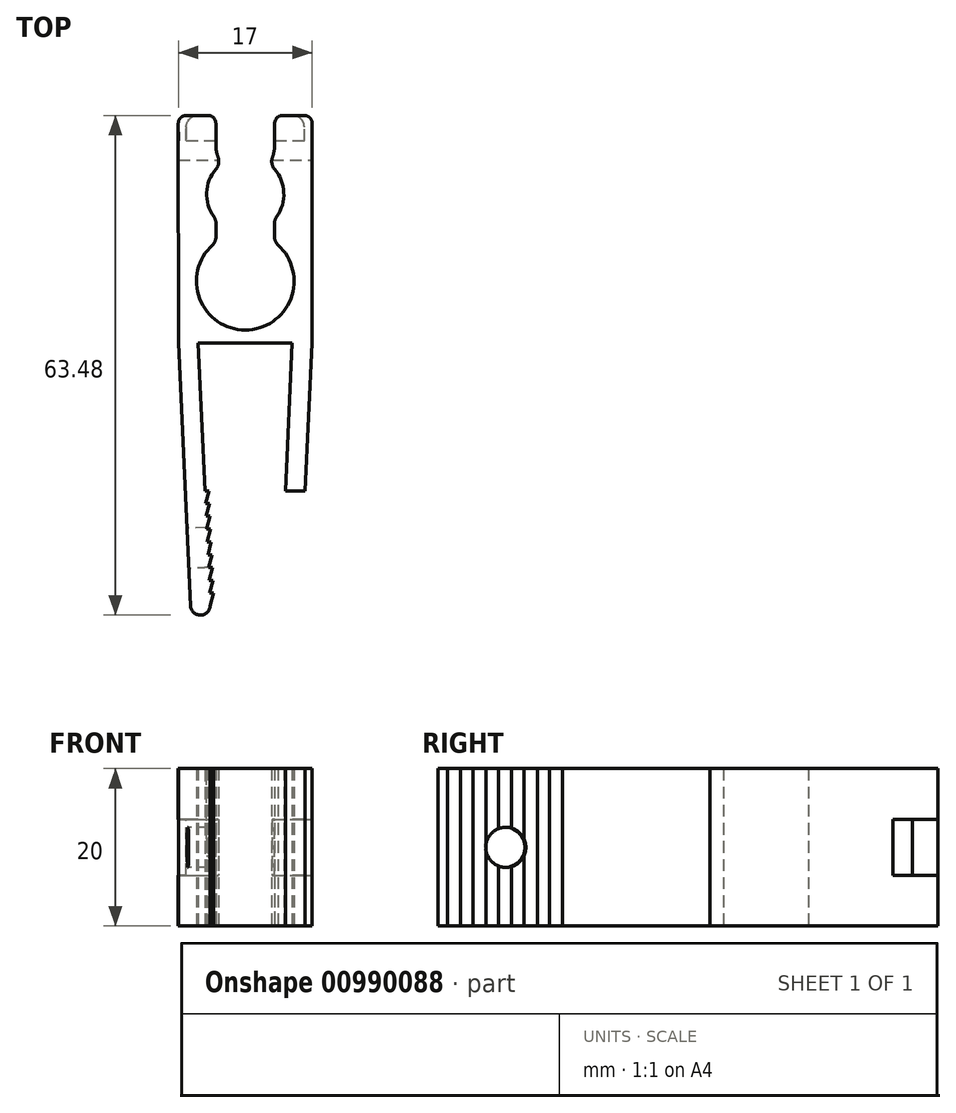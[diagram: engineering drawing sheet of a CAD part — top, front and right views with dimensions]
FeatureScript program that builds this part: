
annotation { "Feature Type Name" : "Feature", "Feature Type Description" : "" }
export const myFeature = defineFeature(function(context is Context, id is Id, definition is map)
    precondition{}
    {
        {
            var Q0;
            Q0=qCreatedBy(makeId("Top.planeOp"),FACE);
            var sketch = newSketch(context, id + "F0", { "sketchPlane" : qUnion([Q0])});
            skPoint(sketch, "E0.MirrorCS.start.orphan", {"position": v(12.82, 0) * mm});
            skLineSegment(sketch, "E1.MirrorCS", {"start": v(-8.47, 46.35) * mm, "end": v(-8.5, 70.8) * mm});
            skPoint(sketch, "E2.MirrorCS.start.orphan", {"position": v(0, 0) * mm});
            skLineSegment(sketch, "E3", {"start": v(0, 49.57) * mm, "end": v(0, 48.03) * mm});
            skLineSegment(sketch, "E4", {"start": v(0, 46.35) * mm, "end": v(5.97, 46.35) * mm});
            skLineSegment(sketch, "E5", {"start": v(0, 46.35) * mm, "end": v(-5.97, 46.35) * mm});
            skLineSegment(sketch, "E6", {"start": v(0, 65.28) * mm, "end": v(0, 49.27) * mm, "construction": true});
            skArc(sketch, "E7", {"start": v(-3.73, 68.46) * mm, "mid": v(-4.9, 65.5) * mm, "end": v(-4, 62.44) * mm});
            skPoint(sketch, "E8.visualSharp", {"position": v(8.5, 0) * mm});
            skPoint(sketch, "E9.visualSharp", {"position": v(-8.5, 0) * mm});
            skLineSegment(sketch, "E10", {"start": v(0, 65.28) * mm, "end": v(0, 75.2) * mm, "construction": true});
            skLineSegment(sketch, "E11.MirrorCS", {"start": v(8.47, 46.35) * mm, "end": v(8.5, 70.8) * mm});
            skPoint(sketch, "E12.orphan", {"position": v(-6, 0) * mm});
            skPoint(sketch, "E13.trimOffspring.start.orphan", {"position": v(6, 0) * mm});
            skPoint(sketch, "E14.visualSharp", {"position": v(-8.5, 10.27) * mm});
            skLineSegment(sketch, "E15", {"start": v(3.71, 61.57) * mm, "end": v(3.71, 59.9) * mm});
            skArc(sketch, "E16.trimOffspring", {"start": v(4, 62.44) * mm, "mid": v(4.9, 65.5) * mm, "end": v(3.73, 68.46) * mm});
            skPoint(sketch, "E17.visualSharp", {"position": v(3.71, 62.08) * mm});
            skArc(sketch, "E17.filletArc", {"start": v(4, 62.44) * mm, "mid": v(3.79, 62.02) * mm, "end": v(3.71, 61.57) * mm});
            skArc(sketch, "E18.filletArc", {"start": v(3.71, 59.9) * mm, "mid": v(3.83, 59.32) * mm, "end": v(4.15, 58.84) * mm});
            skArc(sketch, "E19.MirrorCS", {"start": v(-4, 62.44) * mm, "mid": v(-3.79, 62.02) * mm, "end": v(-3.71, 61.57) * mm});
            skLineSegment(sketch, "E20.MirrorCS", {"start": v(-3.71, 61.57) * mm, "end": v(-3.71, 59.9) * mm});
            skArc(sketch, "E21.MirrorCS", {"start": v(-3.71, 59.9) * mm, "mid": v(-3.83, 59.32) * mm, "end": v(-4.15, 58.84) * mm});
            skArc(sketch, "E22.trimOffspring", {"start": v(-4.15, 58.84) * mm, "mid": v(0, 48.03) * mm, "end": v(4.15, 58.84) * mm});
            skPoint(sketch, "E23.center.orphan", {"position": v(0, 54.53) * mm});
            skArc(sketch, "E24.filletArc", {"start": v(3.74, 70.42) * mm, "mid": v(3.37, 69.45) * mm, "end": v(3.73, 68.46) * mm});
            skArc(sketch, "E25.MirrorCS", {"start": v(-3.45, 69.94) * mm, "mid": v(-3.4, 69.16) * mm, "end": v(-3.73, 68.46) * mm});
            skPoint(sketch, "E26.orphan", {"position": v(-8.47, 46.35) * mm});
            skLineSegment(sketch, "E27", {"start": v(-5.97, 46.35) * mm, "end": v(-5.12, 27.58) * mm});
            skLineSegment(sketch, "E28", {"start": v(-8.47, 46.35) * mm, "end": v(-6.95, 13) * mm});
            skArc(sketch, "E29", {"start": v(-6.95, 13) * mm, "mid": v(-5.7, 11.81) * mm, "end": v(-4.45, 13) * mm});
            skArc(sketch, "E30.MirrorCS", {"start": v(6.95, 13) * mm, "mid": v(5.7, 11.81) * mm, "end": v(4.45, 13) * mm});
            skLineSegment(sketch, "E31.MirrorCS", {"start": v(8.47, 46.35) * mm, "end": v(6.95, 13) * mm});
            skLineSegment(sketch, "E32.MirrorCS", {"start": v(5.97, 46.35) * mm, "end": v(5.12, 27.58) * mm});
            skLineSegment(sketch, "E33", {"start": v(-4.45, 13) * mm, "end": v(-4.03, 14.62) * mm});
            skLineSegment(sketch, "E34", {"start": v(-4.03, 14.62) * mm, "end": v(-4.52, 14.62) * mm});
            skLineSegment(sketch, "E35", {"start": v(-4.52, 14.62) * mm, "end": v(-4.1, 16.24) * mm});
            skLineSegment(sketch, "E36", {"start": v(-4.1, 16.24) * mm, "end": v(-4.59, 16.24) * mm});
            skLineSegment(sketch, "E37", {"start": v(-4.59, 16.24) * mm, "end": v(-4.17, 17.86) * mm});
            skLineSegment(sketch, "E38", {"start": v(-4.17, 17.86) * mm, "end": v(-4.67, 17.86) * mm});
            skLineSegment(sketch, "E39", {"start": v(-4.67, 17.86) * mm, "end": v(-4.25, 19.48) * mm});
            skLineSegment(sketch, "E40", {"start": v(-4.25, 19.48) * mm, "end": v(-4.75, 19.48) * mm});
            skLineSegment(sketch, "E41", {"start": v(-4.75, 19.48) * mm, "end": v(-4.32, 21.1) * mm});
            skLineSegment(sketch, "E42", {"start": v(-4.32, 21.1) * mm, "end": v(-4.82, 21.1) * mm});
            skLineSegment(sketch, "E43", {"start": v(-4.82, 21.1) * mm, "end": v(-4.4, 22.72) * mm});
            skLineSegment(sketch, "E44", {"start": v(-4.4, 22.72) * mm, "end": v(-4.9, 22.72) * mm});
            skLineSegment(sketch, "E45", {"start": v(-4.9, 22.72) * mm, "end": v(-4.47, 24.4) * mm});
            skLineSegment(sketch, "E46", {"start": v(-4.47, 24.4) * mm, "end": v(-4.97, 24.4) * mm});
            skLineSegment(sketch, "E47", {"start": v(-4.97, 24.34) * mm, "end": v(-4.54, 25.96) * mm});
            skLineSegment(sketch, "E48", {"start": v(-4.54, 25.96) * mm, "end": v(-5.04, 25.96) * mm});
            skLineSegment(sketch, "E49", {"start": v(-5.04, 25.96) * mm, "end": v(-4.62, 27.58) * mm});
            skLineSegment(sketch, "E50", {"start": v(-4.62, 27.58) * mm, "end": v(-7.62, 27.58) * mm});
            skLineSegment(sketch, "E51.MirrorCS", {"start": v(4.45, 13) * mm, "end": v(4.03, 14.62) * mm});
            skLineSegment(sketch, "E52.MirrorCS", {"start": v(4.47, 24.4) * mm, "end": v(4.97, 24.4) * mm});
            skLineSegment(sketch, "E53.MirrorCS", {"start": v(4.54, 25.96) * mm, "end": v(5.04, 25.96) * mm});
            skLineSegment(sketch, "E54.MirrorCS", {"start": v(4.17, 17.86) * mm, "end": v(4.67, 17.86) * mm});
            skLineSegment(sketch, "E55.MirrorCS", {"start": v(4.32, 21.1) * mm, "end": v(4.82, 21.1) * mm});
            skLineSegment(sketch, "E56.MirrorCS", {"start": v(4.25, 19.48) * mm, "end": v(4.75, 19.48) * mm});
            skLineSegment(sketch, "E57.MirrorCS", {"start": v(4.4, 22.72) * mm, "end": v(4.9, 22.72) * mm});
            skLineSegment(sketch, "E58.MirrorCS", {"start": v(4.1, 16.24) * mm, "end": v(4.6, 16.24) * mm});
            skLineSegment(sketch, "E59.MirrorCS", {"start": v(4.62, 27.58) * mm, "end": v(7.62, 27.58) * mm});
            skLineSegment(sketch, "E60.MirrorCS", {"start": v(4.82, 21.1) * mm, "end": v(4.4, 22.72) * mm});
            skLineSegment(sketch, "E61.MirrorCS", {"start": v(5.04, 25.96) * mm, "end": v(4.62, 27.58) * mm});
            skLineSegment(sketch, "E62.MirrorCS", {"start": v(4.75, 19.48) * mm, "end": v(4.32, 21.1) * mm});
            skLineSegment(sketch, "E63.MirrorCS", {"start": v(4.53, 14.6) * mm, "end": v(4.1, 16.24) * mm});
            skLineSegment(sketch, "E64.MirrorCS", {"start": v(4.9, 22.72) * mm, "end": v(4.47, 24.4) * mm});
            skLineSegment(sketch, "E65.MirrorCS", {"start": v(4.67, 17.86) * mm, "end": v(4.25, 19.48) * mm});
            skLineSegment(sketch, "E66.MirrorCS", {"start": v(4.6, 16.24) * mm, "end": v(4.17, 17.86) * mm});
            skLineSegment(sketch, "E67.MirrorCS", {"start": v(4.03, 14.62) * mm, "end": v(4.53, 14.62) * mm});
            skLineSegment(sketch, "E68.MirrorCS", {"start": v(4.97, 24.34) * mm, "end": v(4.54, 25.96) * mm});
            skLineSegment(sketch, "E69", {"start": v(-4.74, 75.29) * mm, "end": v(-7.5, 75.29) * mm});
            skLineSegment(sketch, "E70", {"start": v(-8.5, 70.8) * mm, "end": v(-8.5, 74.29) * mm});
            skLineSegment(sketch, "E71", {"start": v(-3.74, 71.6) * mm, "end": v(-3.74, 74.29) * mm});
            skArc(sketch, "E72.filletArc", {"start": v(-3.74, 71.6) * mm, "mid": v(-3.67, 70.76) * mm, "end": v(-3.45, 69.94) * mm});
            skArc(sketch, "E73.MirrorCS", {"start": v(3.74, 71.6) * mm, "mid": v(3.67, 70.76) * mm, "end": v(3.45, 69.94) * mm});
            skLineSegment(sketch, "E74.MirrorCS", {"start": v(8.5, 70.8) * mm, "end": v(8.5, 74.29) * mm});
            skLineSegment(sketch, "E75.MirrorCS", {"start": v(3.74, 71.6) * mm, "end": v(3.74, 74.29) * mm});
            skLineSegment(sketch, "E76.MirrorCS", {"start": v(4.74, 75.29) * mm, "end": v(7.5, 75.29) * mm});
            skPoint(sketch, "E77.visualSharp", {"position": v(-3.74, 75.29) * mm});
            skArc(sketch, "E77.filletArc", {"start": v(-3.74, 74.29) * mm, "mid": v(-4.03, 75) * mm, "end": v(-4.74, 75.29) * mm});
            skPoint(sketch, "E78.visualSharp", {"position": v(3.74, 75.29) * mm});
            skArc(sketch, "E78.filletArc", {"start": v(4.74, 75.29) * mm, "mid": v(4.03, 75) * mm, "end": v(3.74, 74.29) * mm});
            skPoint(sketch, "E79.visualSharp", {"position": v(8.5, 75.29) * mm});
            skArc(sketch, "E79.filletArc", {"start": v(8.5, 74.29) * mm, "mid": v(8.21, 75) * mm, "end": v(7.5, 75.29) * mm});
            skPoint(sketch, "E80.visualSharp", {"position": v(-8.5, 75.29) * mm});
            skArc(sketch, "E80.filletArc", {"start": v(-7.5, 75.29) * mm, "mid": v(-8.21, 75) * mm, "end": v(-8.5, 74.29) * mm});
            skSolve(sketch);
        }
        {
            var Q0;
            {var subQ7=sQuery(id+"F0.wireOp",EDGE,"E1.MirrorCS");Q0=makeQuery(id+"F0.imprint","IMPRINT",FACE,{"disambiguationData":[TD([[makeQuery(id+"F0.imprint","IMPRINT",EDGE,{"derivedFrom":subQ7}),-1.0]])]});}
            var Q1;
            {var subQ8=sQuery(id+"F0.wireOp",EDGE,"E30.MirrorCS");Q1=makeQuery(id+"F0.imprint","IMPRINT",FACE,{"disambiguationData":[TD([[makeQuery(id+"F0.imprint","IMPRINT",EDGE,{"derivedFrom":subQ8}),-1.0]])]});}
            var Q2;
            {var subQ0=sQuery(id+"F0.wireOp",EDGE,"E29");Q2=makeQuery(id+"F0.imprint","IMPRINT",FACE,{"disambiguationData":[TD([[makeQuery(id+"F0.imprint","IMPRINT",EDGE,{"derivedFrom":subQ0}),1.0]])]});}
            extrude(context, id + "F1", {"entities" : qUnion([Q0, Q1, Q2]), "depth" : 20 * mm, "offsetDistance" : 25 * mm});
        }
        {
            var Q0;
            Q0=makeQuery(id+"F1.opExtrude","SWEPT_FACE",FACE,{"disambiguationData":[OSD([sQuery(id+"F0.wireOp",EDGE,"E28")])]});
            cPlane(context, id + "F2", {"entities" : qUnion([Q0]), "cplaneType" : CPlaneType.OFFSET, "offset" : 0 * mm, "width" : 150 * mm, "height" : 150 * mm});
        }
        {
            var Q0;
            Q0=qCreatedBy(id+"F2.planeOp",FACE);
            var sketch = newSketch(context, id + "F3", { "sketchPlane" : qUnion([Q0])});
            skPoint(sketch, "E81", {"position": v(-27.9, 0) * mm});
            skPoint(sketch, "E82", {"position": v(-13.3, 0) * mm});
            skLineSegment(sketch, "E83", {"start": v(-27.9, 0) * mm, "end": v(-27.9, 20) * mm, "construction": true});
            skLineSegment(sketch, "E84", {"start": v(-27.9, 20) * mm, "end": v(-13.3, 0) * mm, "construction": true});
            skLineSegment(sketch, "E85", {"start": v(-13.3, 0) * mm, "end": v(-13.3, 20) * mm});
            skLineSegment(sketch, "E86", {"start": v(-13.3, 20) * mm, "end": v(-27.9, 0) * mm, "construction": true});
            skCircle(sketch, "E87", {"center": v(-20.6, 10) * mm, "radius": 2.55 * mm});
            skSolve(sketch);
        }
        {
            var Q0;
            Q0=makeQuery(id+"F3.imprint","IMPRINT",FACE,{"disambiguationData":[TD([[makeQuery(id+"F3.imprint","IMPRINT",EDGE,{"derivedFrom":sQuery(id+"F3.wireOp",EDGE,"E87")}),1.0]])]});
            extrude(context, id + "F4", {"entities" : qUnion([Q0]), "operationType" : NewBodyOperationType.REMOVE, "oppositeDirection" : true, "depth" : 5 * mm, "offsetDistance" : 25 * mm});
        }
        {
            var Q0;
            Q0=makeQuery(id+"F1.opExtrude","SWEPT_FACE",FACE,{"disambiguationData":[OSD([sQuery(id+"F0.wireOp",EDGE,"E31.MirrorCS")])]});
            cPlane(context, id + "F5", {"entities" : qUnion([Q0]), "cplaneType" : CPlaneType.OFFSET, "offset" : 0 * mm, "width" : 150 * mm, "height" : 150 * mm});
        }
        {
            var Q0;
            Q0=qCreatedBy(id+"F5.planeOp",FACE);
            var sketch = newSketch(context, id + "F6", { "sketchPlane" : qUnion([Q0])});
            skLineSegment(sketch, "E88", {"start": v(13.3, 20) * mm, "end": v(27.9, 0) * mm, "construction": true});
            skLineSegment(sketch, "E89", {"start": v(27.9, 0) * mm, "end": v(27.9, 20) * mm, "construction": true});
            skLineSegment(sketch, "E90", {"start": v(27.9, 20) * mm, "end": v(13.3, 0) * mm, "construction": true});
            skCircle(sketch, "E91", {"center": v(20.6, 10) * mm, "radius": 2.55 * mm});
            skSolve(sketch);
        }
        {
            var Q0;
            Q0=makeQuery(id+"F6.imprint","IMPRINT",FACE,{"disambiguationData":[TD([[makeQuery(id+"F6.imprint","IMPRINT",EDGE,{"derivedFrom":sQuery(id+"F6.wireOp",EDGE,"E91")}),1.0]])]});
            extrude(context, id + "F7", {"entities" : qUnion([Q0]), "operationType" : NewBodyOperationType.REMOVE, "oppositeDirection" : true, "depth" : 3.68 * mm, "offsetDistance" : 25 * mm});
        }
        {
            var Q0;
            Q0=makeQuery(id+"F1.opExtrude","SWEPT_FACE",FACE,{"disambiguationData":[OSD([sQuery(id+"F0.wireOp",EDGE,"E11.MirrorCS"),sQuery(id+"F0.wireOp",EDGE,"E74.MirrorCS")])]});
            cPlane(context, id + "F8", {"entities" : qUnion([Q0]), "cplaneType" : CPlaneType.OFFSET, "offset" : 0 * mm, "width" : 150 * mm, "height" : 150 * mm});
        }
        {
            var Q0;
            Q0=qCreatedBy(id+"F8.planeOp",FACE);
            var sketch = newSketch(context, id + "F9", { "sketchPlane" : qUnion([Q0])});
            skLineSegment(sketch, "E92", {"start": v(75.3, 20) * mm, "end": v(75.3, 0) * mm});
            skLineSegment(sketch, "E93", {"start": v(75.3, 0) * mm, "end": v(46.36, 0) * mm});
            skLineSegment(sketch, "E94", {"start": v(46.36, 0) * mm, "end": v(46.36, 20) * mm});
            skLineSegment(sketch, "E95", {"start": v(46.36, 20) * mm, "end": v(75.3, 20) * mm});
            skLineSegment(sketch, "E96", {"start": v(75.3, 20) * mm, "end": v(46.36, 0) * mm, "construction": true});
            skLineSegment(sketch, "E97", {"start": v(75.3, 0) * mm, "end": v(46.36, 20) * mm, "construction": true});
            skLineSegment(sketch, "E98", {"start": v(75.3, 10) * mm, "end": v(46.36, 10) * mm, "construction": true});
            skLineSegment(sketch, "E99", {"start": v(74.1, 10) * mm, "end": v(74.1, 6.47) * mm});
            skLineSegment(sketch, "E100.MirrorCS", {"start": v(74.1, 10) * mm, "end": v(74.1, 13.53) * mm});
            skPoint(sketch, "E101.start.orphan", {"position": v(75.3, 10) * mm});
            skLineSegment(sketch, "E102", {"start": v(74.1, 10) * mm, "end": v(72.08, 10) * mm});
            skLineSegment(sketch, "E103", {"start": v(72.08, 10) * mm, "end": v(72.08, 13.53) * mm});
            skLineSegment(sketch, "E104", {"start": v(72.08, 13.53) * mm, "end": v(75.3, 13.53) * mm});
            skLineSegment(sketch, "E105.MirrorCS", {"start": v(72.08, 6.47) * mm, "end": v(75.3, 6.47) * mm});
            skLineSegment(sketch, "E106.MirrorCS", {"start": v(72.08, 10) * mm, "end": v(72.08, 6.47) * mm});
            skLineSegment(sketch, "E107", {"start": v(72.08, 6.47) * mm, "end": v(69.6, 6.47) * mm});
            skLineSegment(sketch, "E108", {"start": v(69.6, 6.47) * mm, "end": v(69.6, 13.53) * mm});
            skLineSegment(sketch, "E109", {"start": v(69.6, 13.53) * mm, "end": v(72.08, 13.53) * mm});
            skPoint(sketch, "E110.orphan", {"position": v(74.1, 13.53) * mm});
            skPoint(sketch, "E111.orphan", {"position": v(74.1, 6.47) * mm});
            skPoint(sketch, "E112.end.orphan", {"position": v(75.3, 4) * mm});
            skPoint(sketch, "E112.start.orphan", {"position": v(74.1, 4) * mm});
            skSolve(sketch);
        }
        {
            var Q0;
            Q0=makeQuery(id+"F9.imprint","IMPRINT",FACE,{"disambiguationData":[TD([[makeQuery(id+"F9.imprint","IMPRINT",EDGE,{"derivedFrom":sQuery(id+"F9.wireOp",EDGE,"E103")}),1.0]])]});
            extrude(context, id + "F10", {"entities" : qUnion([Q0]), "operationType" : NewBodyOperationType.REMOVE, "oppositeDirection" : true, "depth" : 20 * mm, "offsetDistance" : 25 * mm});
        }
        {
            var Q0;
            {var subQ0=sQuery(id+"F9.wireOp",EDGE,"E102");Q0=makeQuery(id+"F9.imprint","IMPRINT",FACE,{"disambiguationData":[TD([[makeQuery(id+"F9.imprint","IMPRINT",EDGE,{"derivedFrom":subQ0}),-1.0]])]});}
            var Q1;
            {var subQ0=sQuery(id+"F9.wireOp",EDGE,"E102");Q1=makeQuery(id+"F9.imprint","IMPRINT",FACE,{"disambiguationData":[TD([[makeQuery(id+"F9.imprint","IMPRINT",EDGE,{"derivedFrom":subQ0}),1.0]])]});}
            var Q2;
            {var subQ4=sQuery(id+"F9.wireOp",EDGE,"E99");Q2=makeQuery(id+"F9.imprint","IMPRINT",FACE,{"disambiguationData":[TD([[makeQuery(id+"F9.imprint","IMPRINT",EDGE,{"derivedFrom":subQ4}),1.0]])]});}
            extrude(context, id + "F11", {"entities" : qUnion([Q0, Q1, Q2]), "operationType" : NewBodyOperationType.REMOVE, "oppositeDirection" : true, "depth" : 1 * mm, "offsetDistance" : 25 * mm});
        }
        {
            var Q0;
            Q0=makeQuery(id+"F11.boolean.opBoolean","MERGE",EDGE,{"derivedFrom":[makeQuery(id+"F1.opExtrude","SWEPT_EDGE",EDGE,{"disambiguationData":[OSD([sQuery(id+"F0.wireOp",EDGE,"E76.MirrorCS"),sQuery(id+"F0.wireOp",EDGE,"E79.filletArc")])]})],"fromTools":[makeQuery(id+"F11.opExtrude","CAP_EDGE",EDGE,{"disambiguationData":[OSD([sQuery(id+"F9.wireOp",EDGE,"E92")])],"isStart":false})]});
            fillet(context, id + "F12", {"entities" : qUnion([Q0]), "radius" : 1.5 * mm, "tangentPropagation" : true, "allowEdgeOverflow" : false});
        }
        {
            var Q0;
            Q0=makeQuery(id+"F1.opExtrude","SWEPT_FACE",FACE,{"disambiguationData":[OSD([sQuery(id+"F0.wireOp",EDGE,"E1.MirrorCS"),sQuery(id+"F0.wireOp",EDGE,"E70")])]});
            var sketch = newSketch(context, id + "F13", { "sketchPlane" : qUnion([Q0])});
            skLineSegment(sketch, "E113", {"start": v(-72.1, 13.53) * mm, "end": v(-75.3, 13.53) * mm});
            skPoint(sketch, "E113.endSnap0", {"position": v(-70.86, 13.53) * mm});
            skLineSegment(sketch, "E114", {"start": v(-75.3, 13.53) * mm, "end": v(-75.3, 6.47) * mm});
            skLineSegment(sketch, "E115", {"start": v(-75.3, 6.47) * mm, "end": v(-72.1, 6.47) * mm});
            skLineSegment(sketch, "E116", {"start": v(-72.1, 6.47) * mm, "end": v(-72.1, 13.53) * mm});
            skLineSegment(sketch, "E117", {"start": v(-75.3, 13.53) * mm, "end": v(-72.1, 13.53) * mm});
            skLineSegment(sketch, "E118", {"start": v(-72.1, 6.47) * mm, "end": v(-75.3, 6.47) * mm});
            skSolve(sketch);
        }
        {
            var Q0;
            {var subQ0=sQuery(id+"F13.wireOp",EDGE,"E114");Q0=makeQuery(id+"F13.imprint","IMPRINT",FACE,{"disambiguationData":[TD([[makeQuery(id+"F13.imprint","IMPRINT",EDGE,{"derivedFrom":subQ0}),1.0]])]});}
            var Q1;
            {var subQ0=sQuery(id+"F13.wireOp",EDGE,"E116");Q1=makeQuery(id+"F13.imprint","IMPRINT",FACE,{"disambiguationData":[TD([[makeQuery(id+"F13.imprint","IMPRINT",EDGE,{"derivedFrom":subQ0}),1.0]])]});}
            extrude(context, id + "F14", {"entities" : qUnion([Q0, Q1]), "operationType" : NewBodyOperationType.REMOVE, "oppositeDirection" : true, "depth" : 1 * mm, "offsetDistance" : 25 * mm});
        }
        {
            var Q0;
            Q0=makeQuery(id+"F14.boolean.opBoolean","MERGE",EDGE,{"derivedFrom":[makeQuery(id+"F1.opExtrude","SWEPT_EDGE",EDGE,{"disambiguationData":[OSD([sQuery(id+"F0.wireOp",EDGE,"E69"),sQuery(id+"F0.wireOp",EDGE,"E80.filletArc")])]})],"fromTools":[makeQuery(id+"F14.opExtrude","CAP_EDGE",EDGE,{"disambiguationData":[OSD([sQuery(id+"F13.wireOp",EDGE,"E114")])],"isStart":false})]});
            fillet(context, id + "F15", {"entities" : qUnion([Q0]), "radius" : 1.5 * mm, "tangentPropagation" : true, "allowEdgeOverflow" : false});
        }
    });
